# Revit family: IS_Joy_BC785_BIM_GB
name_source: partatom
category: Plumbing Fixtures
revit_build: Autodesk Revit 2017 (Build: 20160225_1515(x64)
units: mm (PartAtom-declared; Revit-internal decimal feet)

## family parameters
Always vertical = No
Cut with Voids When Loaded = No
OmniClass Number = 23.45.55.17
OmniClass Title = Mixing Faucets
Part Type = Normal
Room Calculation Point = No
Round Connector Dimension = Use Diameter
Shared = No
Work Plane-Based = No

## types (4) — shared parameters
Accessories = https://www.idealstandard.co.uk
AssetType = Fixed
BIMObjectName = ISI_IdealStandard_Shower manual water supply sets_Joy_BC785
BarCode = 3800861086949
Brand = Ideal Standard
CurrencyUnit = £
Description = JOY Single lever shower mixer with backflow preventer. Available in four different finishes, Chrome (AA), Silver storm (GN) 386, Brushed gold (A2) and Magnetic grey (A5)
DistributedBy = Ideal Standard
DurationUnit = Years
ExpectedLife = 30
FaucetFunction = MIXED
FaucetOperation = OTHER
FaucetType = OTHER
Features = Single lever shower mixer with backflow preventer. Available in four different finishes, Chrome (AA), Silver storm (GN) 386, Brushed gold (A2) and Magnetic grey (A5)
Help = https://www.idealstandard.co.uk
IfcExportAs = IfcValveType
IfcExportType = FAUCET
Installation instructions = https://www.idealspec.co.uk
InstallationInstructions = https://www.idealstandard.co.uk
IsBuiltIn = No
MaintenanceInformation = https://www.idealstandard.co.uk
Manufacturer = Ideal Standard
ManufacturerURL = https://www.idealstandard.co.uk
Material = Brass
ModelNumber = BC785
NBS Reference Code = 45-35-70/335
NBS Reference Description = Shower mixers
Name = Shower manual water supply sets_Joy_BC785_IdealStandard
NettWeight = 9
NominalDepth = 343 mm  [stored 1.12533 ft]
NominalHeight = 163 mm  [stored 0.534777 ft]
NominalLength = 343 mm  [stored 1.12533 ft]
NominalWidth = 78 mm  [stored 0.255906 ft]
Product certification = https://www.idealstandard.co.uk
Product group = SHOWER MIXERS
ProductInformation = https://www.idealspec.co.uk
Shape = Sculptured
Size = 307 x 101 x 108 mm
Space = Internal
SpareParts = https://www.idealspec.co.uk
SustainabilityPerformance = https://www.idealspec.co.uk
TestPressure = 10 Bar
URL = https://www.idealstandard.co.uk
Uniclass 2015 Code = Pr_40_20_87_78
Uniclass 2015 Name = Shower manual water supply sets
Uniclass2015Code = Pr_40_20_87_78
Uniclass2015Title = Shower manual water supply sets
Uniclass2015Version = v1.1
Version = 1
VolumeUnits = Litres
WRASURL = https://www.wras.co.uk
WarrantyDescription = Manufacturers Warranty
WarrantyDurationParts = 5
WarrantyDurationUnit = year
WarrantyGuarantorParts = https://www.idealspec.co.uk
WorkingPressure = 3bar
zero-valued in all types: InletConnectionSize, MaterialThickness

## per-type parameters (varying)
| type | Color | Finish | MainColor | Model | ModelReference |
| BC785A2 - JOY SHR MXR EXPSD BR GOLD | Brushed Gold | Brushed Gold | Brushed Gold | BC785A2 | BC785A2 |
| BC785A5 - JOY SHR MXR EXPSD MGN GREY | Brushed Gold | Brushed Gold | Brushed Gold | BC785A2 | BC785A2 |
| BC785AA - JOY SHR MXR EXPSD CHR | Chrome | Chrome | Chrome | BC785AA | BC785AA |
| BC785GN - JOY SHR MXR EXPSD SILV STORM | Silver storm | Silver storm | Silver storm | BC785GN | BC785GN |

note: [stored X ft] marks values corroborated as IEEE doubles in the binary element streams (Revit-internal decimal feet)

## geometry (parser evidence)
native form markers: Sweep x3
no freeform markers — native parametric forms only
